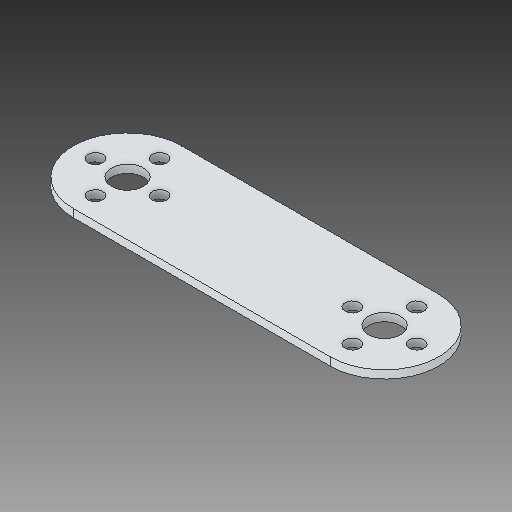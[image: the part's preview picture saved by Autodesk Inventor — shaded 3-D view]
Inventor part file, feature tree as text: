
AUTODESK INVENTOR PART (.ipt)
format: ipt  version: 2018 (Build 220112000, 112)  size: 131,584 bytes
history: native  units: in
note: dims shown in document units (in); Inventor stores cm internally (conversion verified against a paired STEP export)
features: fillet x1
ambient origin geometry x8: Origin, YZ Plane, XZ Plane, XY Plane, X Axis, Y Axis, Z Axis, Center Point
bodies: Solid1 (feature_tree)
feature tree (1):
  fillet  "Fillet1"  [1 undecoded]
note: 1 required parameter value undecoded (feature->parameter linkage not recoverable at this tier; creation-order binding heuristic only, values carry confidence <= 0.55)
